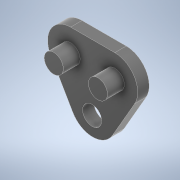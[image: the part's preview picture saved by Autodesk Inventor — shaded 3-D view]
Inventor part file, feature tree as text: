
AUTODESK INVENTOR PART (.ipt)
format: ipt  version: 2022 (Build 260153000, 153)  size: 301,056 bytes
history: native  units: in
note: dims shown in document units (in); Inventor stores cm internally (conversion verified against a paired STEP export)
features: extrude x2, sketch x2, other x1
ambient origin geometry x8: Origin, YZ Plane, XZ Plane, XY Plane, X Axis, Y Axis, Z Axis, Center Point
bodies: Body1 (feature_tree)
feature tree (5):
  other  "Sólido1"
  extrude  "Extrusión1"  Depth=0.0984in
  extrude  "Extrusión2"  Depth=0.0866in
  sketch  "Boceto1"  dims[d2=0.0984in d9=0.0984in]
  sketch  "Boceto3"  dims[d10=0.2496in d13=0.0984in d14=0.2157in d15=0.1228in d16=60.0deg d17=60.0deg d18=60.0deg d19=0.1181in d20=0.0591in d21=0.0in d22=0.0984in d23=0.0984in d24=0.0866in d25=0.0in]
